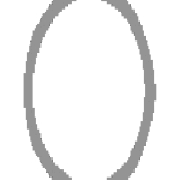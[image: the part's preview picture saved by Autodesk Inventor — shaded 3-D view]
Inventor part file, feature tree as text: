
AUTODESK INVENTOR PART (.ipt)
format: ipt  version: 2021 (Build 250183000, 183)  size: 146,432 bytes
history: native  units: in
note: dims shown in document units (in); Inventor stores cm internally (conversion verified against a paired STEP export)
features: other x5, sketch x2, sweep x1, plane x1
ambient origin geometry x8: Origin, YZ Plane, XZ Plane, XY Plane, X Axis, Y Axis, Z Axis, Center Point
bodies: Solid1 (feature_tree), Body (feature_tree)
feature tree (9):
  other  "Driven Length"
  other  "Frame Generator"
  other  "Start Plane"
  other  "End Plane"
  sweep  "Sweep Path"
  other  "Orientation Work Plane"
  sketch  "Sketch2"  dims[d0=1.0in d1=0.065in]
  plane  "Work Plane3"
  sketch  "Sketch3"  dims[d2=1.1738in d4=-0.0in d5=1.1738in d8=90.0deg d9=1.1738in d10=0.0in d11=0.0in]
